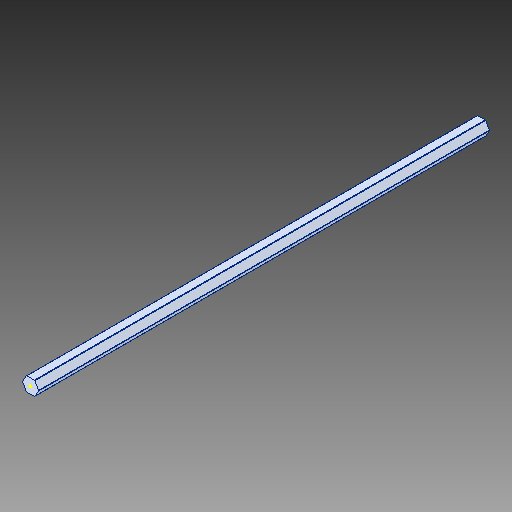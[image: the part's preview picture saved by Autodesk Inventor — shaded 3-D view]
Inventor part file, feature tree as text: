
AUTODESK INVENTOR PART (.ipt)
format: ipt  version: 2017 (Build 210142000, 142)  size: 148,992 bytes
history: native  units: in
note: dims shown in document units (in); Inventor stores cm internally (conversion verified against a paired STEP export)
features: sketch x6, split x1, fillet x1
ambient origin geometry x8: Origin, YZ Plane, XZ Plane, XY Plane, X Axis, Y Axis, Z Axis, Center Point
bodies: Solid1 (feature_tree)
feature tree (8):
  sketch  "Sketch1"  dims[d11=16.0in]
  split  "Split1"
  sketch  "Sketch3"  dims[d13=7.8125in]
  sketch  "Sketch4"  dims[d14=3.5453in]
  sketch  "Sketch5"  dims[d15=3.5453in]
  sketch  "Sketch6"
  sketch  "Sketch2"  dims[d12=7.8125in]
  fillet  "Fillet1"  Radius=8.5in
